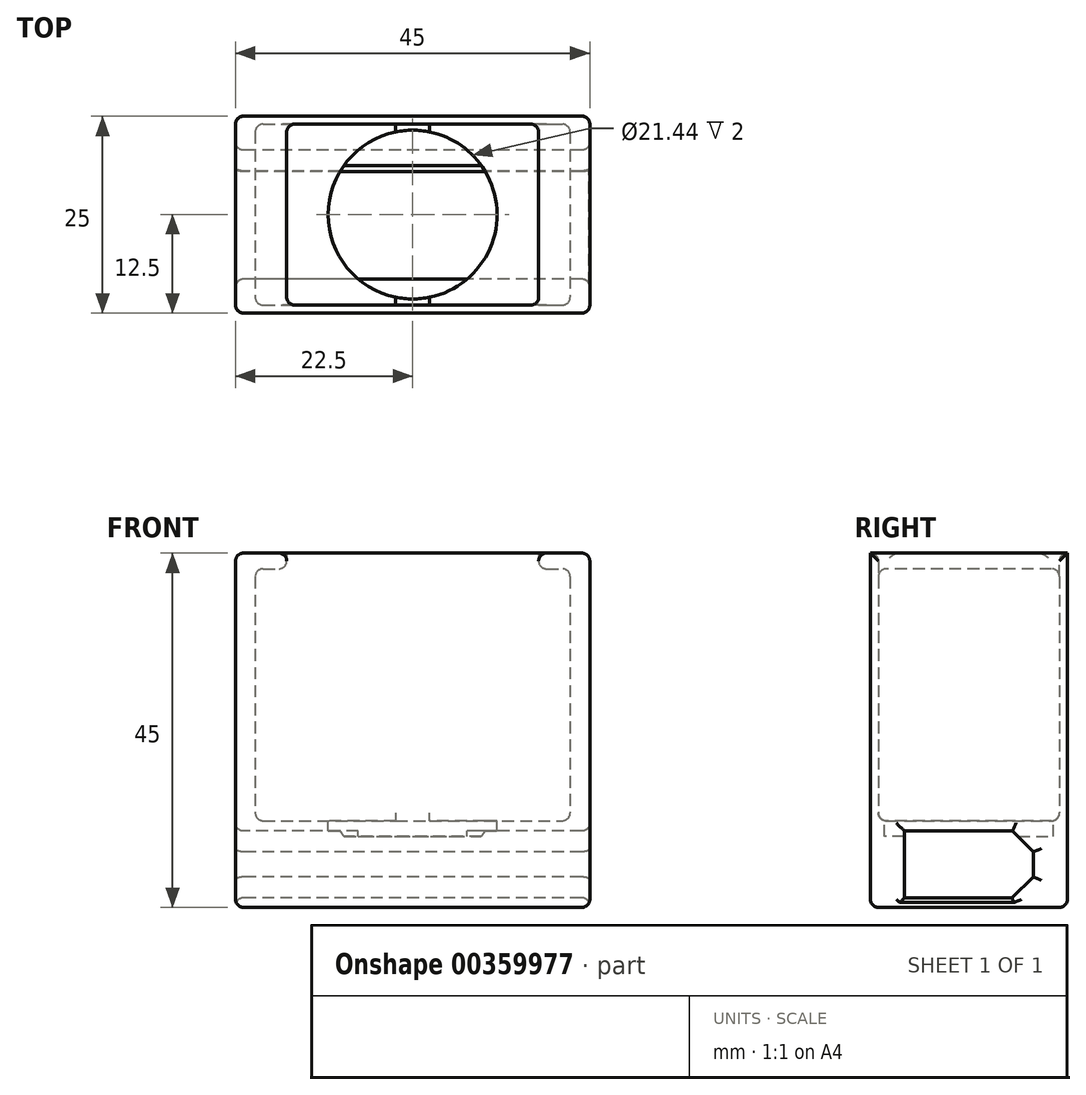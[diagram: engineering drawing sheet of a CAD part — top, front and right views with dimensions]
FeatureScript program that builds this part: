
annotation { "Feature Type Name" : "Feature", "Feature Type Description" : "" }
export const myFeature = defineFeature(function(context is Context, id is Id, definition is map)
    precondition{}
    {
        {
            var Q0;
            Q0=qCreatedBy(makeId("Top.planeOp"),FACE);
            var sketch = newSketch(context, id + "F0", { "sketchPlane" : qUnion([Q0])});
            skLineSegment(sketch, "E0", {"start": v(-22.5, 12.5) * mm, "end": v(22.5, 12.5) * mm});
            skLineSegment(sketch, "E1", {"start": v(22.5, 12.5) * mm, "end": v(22.5, -12.5) * mm});
            skLineSegment(sketch, "E2.MirrorCS", {"start": v(-22.5, -12.5) * mm, "end": v(22.5, -12.5) * mm});
            skLineSegment(sketch, "E3.MirrorCS", {"start": v(-22.5, 12.5) * mm, "end": v(-22.5, -12.5) * mm});
            skLineSegment(sketch, "E4", {"start": v(-20, 11.5) * mm, "end": v(20, 11.5) * mm});
            skLineSegment(sketch, "E5", {"start": v(20, 11.5) * mm, "end": v(20, -11.5) * mm});
            skLineSegment(sketch, "E6.MirrorCS", {"start": v(-20, 11.5) * mm, "end": v(-20, -11.5) * mm});
            skLineSegment(sketch, "E7.MirrorCS", {"start": v(-20, -11.5) * mm, "end": v(20, -11.5) * mm});
            skLineSegment(sketch, "E8", {"start": v(16, 11.5) * mm, "end": v(16, -11.5) * mm});
            skLineSegment(sketch, "E9.MirrorCS", {"start": v(-16, 11.5) * mm, "end": v(-16, -11.5) * mm});
            skSolve(sketch);
        }
        {
            var Q0;
            Q0=makeQuery(id+"F0.imprint","IMPRINT",FACE,{"disambiguationData":[TD([[makeQuery(id+"F0.imprint","IMPRINT",EDGE,{"derivedFrom":sQuery(id+"F0.wireOp",EDGE,"E4")}),-1.0]])]});
            extrude(context, id + "F1", {"entities" : qUnion([Q0]), "depth" : 11 * mm});
        }
        {
            var Q0;
            Q0=makeQuery(id+"F0.imprint","IMPRINT",FACE,{"disambiguationData":[TD([[makeQuery(id+"F0.imprint","IMPRINT",EDGE,{"derivedFrom":sQuery(id+"F0.wireOp",EDGE,"E0")}),-1.0]])]});
            extrude(context, id + "F2", {"entities" : qUnion([Q0]), "operationType" : NewBodyOperationType.ADD, "depth" : 45 * mm});
        }
        {
            var Q0;
            Q0=makeQuery(id+"F2.opExtrude","SWEPT_FACE",FACE,{"disambiguationData":[OSD([sQuery(id+"F0.wireOp",EDGE,"E3.MirrorCS")])]});
            var sketch = newSketch(context, id + "F3", { "sketchPlane" : qUnion([Q0])});
            skLineSegment(sketch, "E10", {"start": v(-5.46, 1.2) * mm, "end": v(8.2, 1.2) * mm});
            skLineSegment(sketch, "E11.0", {"start": v(-5.55, 9.7) * mm, "end": v(8.2, 9.7) * mm});
            skLineSegment(sketch, "E12", {"start": v(8.2, 9.7) * mm, "end": v(8.2, 1.2) * mm});
            skLineSegment(sketch, "E13.MirrorCS", {"start": v(-8.2, 7.05) * mm, "end": v(-8.2, 3.85) * mm});
            skPoint(sketch, "E14.orphan", {"position": v(8.2, 14.67) * mm});
            skPoint(sketch, "E15.orphan", {"position": v(-8.2, 14.67) * mm});
            skPoint(sketch, "E16.orphan", {"position": v(-8.2, -8.48) * mm});
            skPoint(sketch, "E17.orphan", {"position": v(8.2, -8.48) * mm});
            skLineSegment(sketch, "E18", {"start": v(-5.55, 9.7) * mm, "end": v(-8.2, 7.05) * mm});
            skLineSegment(sketch, "E19.MirrorCS", {"start": v(-5.46, 1.2) * mm, "end": v(-8.2, 3.85) * mm});
            skPoint(sketch, "E20.orphan", {"position": v(-3.22, 12.03) * mm});
            skPoint(sketch, "E21.trimOffspring.end.orphan", {"position": v(-10.33, 4.83) * mm});
            skPoint(sketch, "E22.trimOffspring.end.orphan", {"position": v(-10.33, 6.07) * mm});
            skPoint(sketch, "E23.start.orphan", {"position": v(-8.2, 5.45) * mm});
            skPoint(sketch, "E24.orphan", {"position": v(-8.2, 1.2) * mm});
            skPoint(sketch, "E25.orphan", {"position": v(-8.2, 9.7) * mm});
            skSolve(sketch);
        }
        {
            var Q0;
            Q0=makeQuery(id+"F3.imprint","IMPRINT",FACE,{"disambiguationData":[TD([[makeQuery(id+"F3.imprint","IMPRINT",EDGE,{"derivedFrom":sQuery(id+"F3.wireOp",EDGE,"E10")}),1.0]])]});
            extrude(context, id + "F4", {"entities" : qUnion([Q0]), "operationType" : NewBodyOperationType.REMOVE, "endBound" : BoundingType.THROUGH_ALL, "oppositeDirection" : true, "depth" : 25 * mm});
        }
        {
            var Q0;
            Q0=makeQuery(id+"F2.opExtrude","SWEPT_FACE",FACE,{"disambiguationData":[OSD([sQuery(id+"F0.wireOp",EDGE,"E1")])]});
            var Q1;
            Q1=makeQuery(id+"F2.opExtrude","SWEPT_FACE",FACE,{"disambiguationData":[OSD([sQuery(id+"F0.wireOp",EDGE,"E3.MirrorCS")])]});
            var Q2;
            Q2=makeQuery(id+"F2.opExtrude","CAP_EDGE",EDGE,{"disambiguationData":[OSD([sQuery(id+"F0.wireOp",EDGE,"E0")])],"isStart":true});
            var Q3;
            Q3=makeQuery(id+"F2.opExtrude","CAP_EDGE",EDGE,{"disambiguationData":[OSD([sQuery(id+"F0.wireOp",EDGE,"E2.MirrorCS")])],"isStart":true});
            fillet(context, id + "F5", {"entities" : qUnion([Q0, Q1, Q2, Q3]), "radius" : 1 * mm, "tangentPropagation" : true, "allowEdgeOverflow" : false});
        }
        {
            var Q0;
            Q0=makeQuery(id+"F1.opExtrude","CAP_FACE",FACE,{"disambiguationData":[OSD([sQuery(id+"F0.wireOp",EDGE,"E4"),sQuery(id+"F0.wireOp",EDGE,"E5"),sQuery(id+"F0.wireOp",EDGE,"E6.MirrorCS"),sQuery(id+"F0.wireOp",EDGE,"E7.MirrorCS")])],"isStart":false});
            var sketch = newSketch(context, id + "F6", { "sketchPlane" : qUnion([Q0])});
            skCircle(sketch, "E26", {"center": v(0, 0) * mm, "radius": 10.72 * mm});
            skSolve(sketch);
        }
        {
            var Q0;
            Q0=makeQuery(id+"F6.imprint","IMPRINT",FACE,{"disambiguationData":[TD([[makeQuery(id+"F6.imprint","IMPRINT",EDGE,{"derivedFrom":sQuery(id+"F6.wireOp",EDGE,"E26")}),1.0]])]});
            extrude(context, id + "F7", {"entities" : qUnion([Q0]), "operationType" : NewBodyOperationType.REMOVE, "oppositeDirection" : true, "depth" : 2 * mm});
        }
        {
            var Q0;
            {var subQ0=sQuery(id+"F0.wireOp",EDGE,"E6.MirrorCS");Q0=makeQuery(id+"F0.imprint","IMPRINT",FACE,{"disambiguationData":[TD([[makeQuery(id+"F0.imprint","IMPRINT",EDGE,{"derivedFrom":subQ0}),1.0]])]});}
            var Q1;
            {var subQ0=sQuery(id+"F0.wireOp",EDGE,"E5");Q1=makeQuery(id+"F0.imprint","IMPRINT",FACE,{"disambiguationData":[TD([[makeQuery(id+"F0.imprint","IMPRINT",EDGE,{"derivedFrom":subQ0}),-1.0]])]});}
            extrude(context, id + "F8", {"entities" : qUnion([Q0, Q1]), "operationType" : NewBodyOperationType.ADD, "depth" : 45 * mm, "hasSecondDirection" : true, "secondDirectionOppositeDirection" : false, "secondDirectionDepth" : 43 * mm});
        }
        {
            var Q0;
            Q0=makeQuery(id+"F2.opExtrude","SWEPT_FACE",FACE,{"disambiguationData":[OSD([sQuery(id+"F0.wireOp",EDGE,"E6.MirrorCS")])]});
            var Q1;
            Q1=makeQuery(id+"F2.opExtrude","SWEPT_FACE",FACE,{"disambiguationData":[OSD([sQuery(id+"F0.wireOp",EDGE,"E4")])]});
            var Q2;
            Q2=makeQuery(id+"F2.opExtrude","SWEPT_FACE",FACE,{"disambiguationData":[OSD([sQuery(id+"F0.wireOp",EDGE,"E7.MirrorCS")])]});
            var Q3;
            Q3=makeQuery(id+"F2.opExtrude","SWEPT_FACE",FACE,{"disambiguationData":[OSD([sQuery(id+"F0.wireOp",EDGE,"E5")])]});
            var Q4;
            Q4=makeQuery(id+"F8.opExtrude","CAP_EDGE",EDGE,{"disambiguationData":[OSD([sQuery(id+"F0.wireOp",EDGE,"E8")])],"isStart":true});
            var Q5;
            Q5=makeQuery(id+"F8.opExtrude","CAP_EDGE",EDGE,{"disambiguationData":[OSD([sQuery(id+"F0.wireOp",EDGE,"E9.MirrorCS")])],"isStart":true});
            fillet(context, id + "F9", {"entities" : qUnion([Q0, Q1, Q2, Q3, Q4, Q5]), "radius" : 1 * mm, "tangentPropagation" : true, "allowEdgeOverflow" : false});
        }
    });
